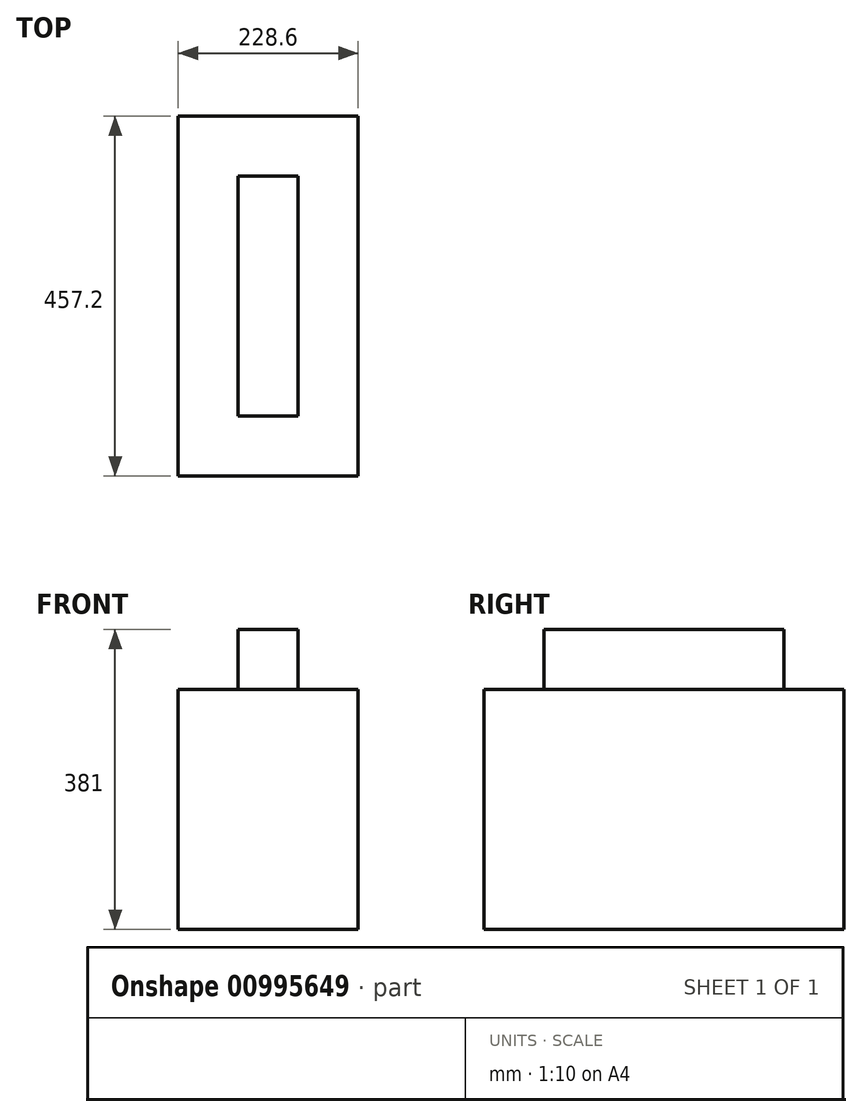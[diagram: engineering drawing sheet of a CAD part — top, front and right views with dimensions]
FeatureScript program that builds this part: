
annotation { "Feature Type Name" : "Feature", "Feature Type Description" : "" }
export const myFeature = defineFeature(function(context is Context, id is Id, definition is map)
    precondition{}
    {
        {
            var Q0;
            Q0=qCreatedBy(makeId("Top.planeOp"),FACE);
            var sketch = newSketch(context, id + "F0", { "sketchPlane" : qUnion([Q0])});
            skLineSegment(sketch, "E0.bottom", {"start": v(-228.6, -228.6) * mm, "end": v(0, -228.6) * mm});
            skLineSegment(sketch, "E0.top", {"start": v(-228.6, 228.6) * mm, "end": v(0, 228.6) * mm});
            skLineSegment(sketch, "E0.left", {"start": v(-228.6, -228.6) * mm, "end": v(-228.6, 228.6) * mm});
            skLineSegment(sketch, "E0.right", {"start": v(0, -228.6) * mm, "end": v(0, 228.6) * mm});
            skPoint(sketch, "E1", {"position": v(0, 0) * mm});
            skSolve(sketch);
        }
        {
            var Q0;
            Q0=makeQuery(id+"F0.imprint","IMPRINT",FACE,{"disambiguationData":[TD([[makeQuery(id+"F0.imprint","IMPRINT",EDGE,{"derivedFrom":sQuery(id+"F0.wireOp",EDGE,"E0.bottom")}),1.0]])]});
            extrude(context, id + "F1", {"entities" : qUnion([Q0]), "depth" : 304.8 * mm, "offsetDistance" : 25.4 * mm});
        }
        {
            var Q0;
            Q0=makeQuery(id+"F1.opExtrude","CAP_FACE",FACE,{"disambiguationData":[OSD([sQuery(id+"F0.wireOp",EDGE,"E0.bottom"),sQuery(id+"F0.wireOp",EDGE,"E0.top"),sQuery(id+"F0.wireOp",EDGE,"E0.left"),sQuery(id+"F0.wireOp",EDGE,"E0.right")])],"isStart":false});
            var sketch = newSketch(context, id + "F2", { "sketchPlane" : qUnion([Q0])});
            skLineSegment(sketch, "E2", {"start": v(-228.6, 228.6) * mm, "end": v(0, -228.6) * mm, "construction": true});
            skPoint(sketch, "E3", {"position": v(-114.3, 0) * mm});
            skLineSegment(sketch, "E4.bottom", {"start": v(-76.2, -152.4) * mm, "end": v(-152.4, -152.4) * mm});
            skLineSegment(sketch, "E4.top", {"start": v(-76.2, 152.4) * mm, "end": v(-152.4, 152.4) * mm});
            skLineSegment(sketch, "E4.left", {"start": v(-76.2, -152.4) * mm, "end": v(-76.2, 152.4) * mm});
            skLineSegment(sketch, "E4.right", {"start": v(-152.4, -152.4) * mm, "end": v(-152.4, 152.4) * mm});
            skSolve(sketch);
        }
        {
            var Q0;
            Q0=makeQuery(id+"F2.imprint","IMPRINT",FACE,{"disambiguationData":[TD([[makeQuery(id+"F2.imprint","IMPRINT",EDGE,{"derivedFrom":sQuery(id+"F2.wireOp",EDGE,"E4.bottom")}),-1.0]])]});
            extrude(context, id + "F3", {"entities" : qUnion([Q0]), "operationType" : NewBodyOperationType.ADD, "depth" : 76.2 * mm, "offsetDistance" : 25.4 * mm});
        }
    });
